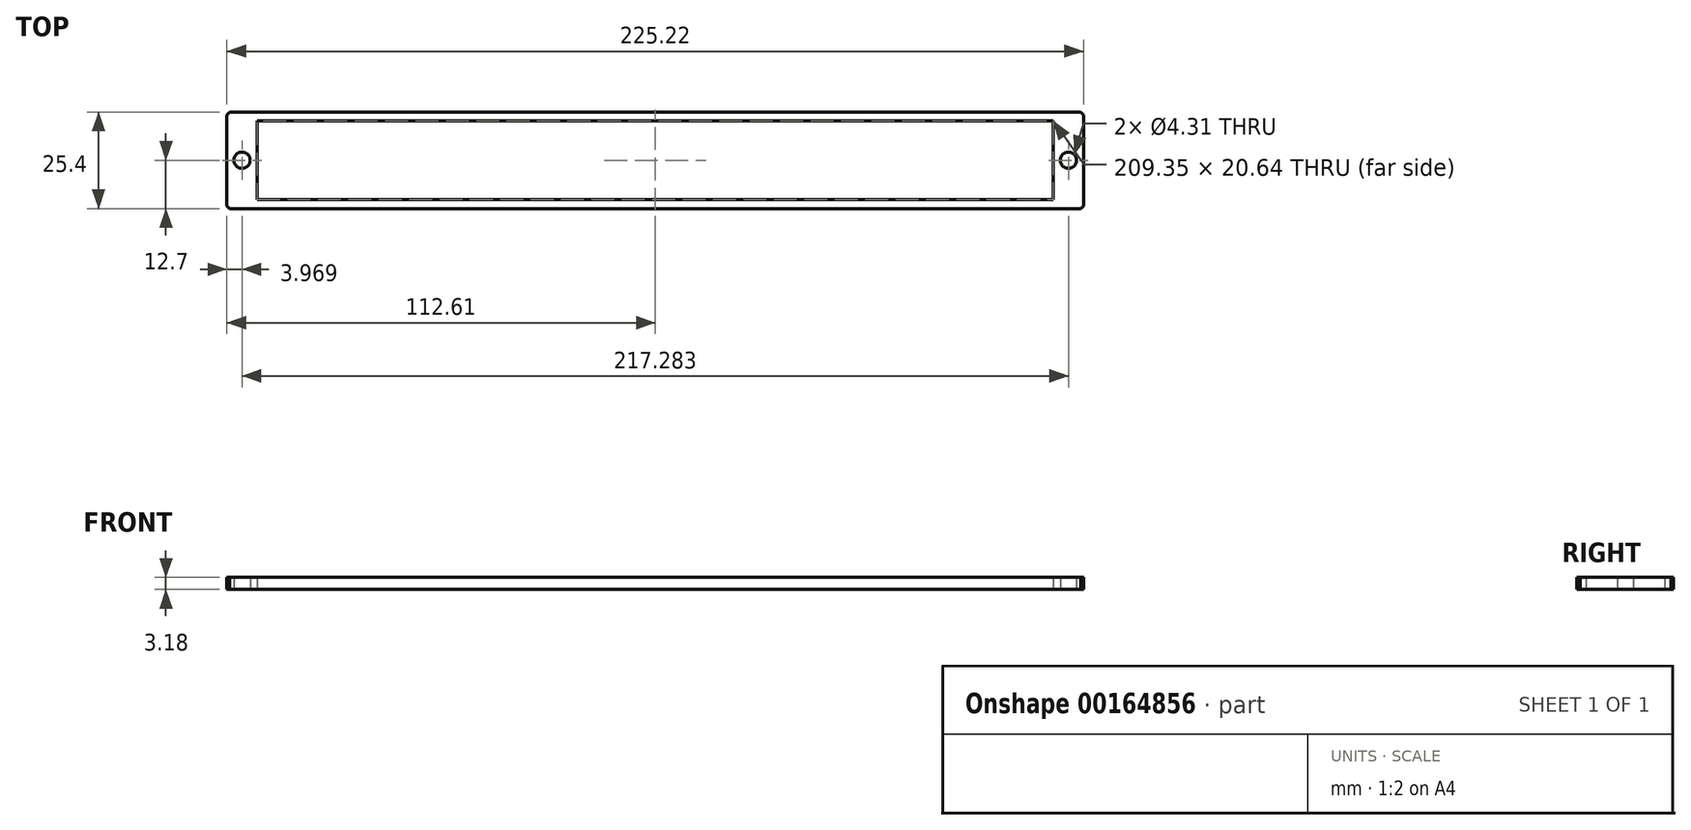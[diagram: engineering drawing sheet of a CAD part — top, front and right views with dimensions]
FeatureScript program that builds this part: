
annotation { "Feature Type Name" : "Feature", "Feature Type Description" : "" }
export const myFeature = defineFeature(function(context is Context, id is Id, definition is map)
    precondition{}
    {
        {
            var Q0;
            Q0=qCreatedBy(makeId("Top.planeOp"),FACE);
            var sketch = newSketch(context, id + "F0", { "sketchPlane" : qUnion([Q0])});
            skLineSegment(sketch, "E0.bottom", {"start": v(104.67, 10.32) * mm, "end": v(-104.67, 10.32) * mm});
            skLineSegment(sketch, "E0.top", {"start": v(104.67, -10.32) * mm, "end": v(-104.67, -10.32) * mm});
            skLineSegment(sketch, "E0.left", {"start": v(104.67, 10.32) * mm, "end": v(104.67, -10.32) * mm});
            skLineSegment(sketch, "E0.right", {"start": v(-104.67, 10.32) * mm, "end": v(-104.67, -10.32) * mm});
            skPoint(sketch, "E0.middle", {"position": v(0, 0) * mm});
            skLineSegment(sketch, "E1.bottom", {"start": v(112.61, 12.7) * mm, "end": v(-112.61, 12.7) * mm});
            skLineSegment(sketch, "E1.top", {"start": v(112.61, -12.7) * mm, "end": v(-112.61, -12.7) * mm});
            skLineSegment(sketch, "E1.left", {"start": v(112.61, 12.7) * mm, "end": v(112.61, -12.7) * mm});
            skLineSegment(sketch, "E1.right", {"start": v(-112.61, 12.7) * mm, "end": v(-112.61, -12.7) * mm});
            skLineSegment(sketch, "E2", {"start": v(-112.61, 0) * mm, "end": v(-108.64, 0) * mm, "construction": true});
            skLineSegment(sketch, "E3", {"start": v(-108.64, 0) * mm, "end": v(-104.67, 0) * mm, "construction": true});
            skLineSegment(sketch, "E4", {"start": v(104.67, 0) * mm, "end": v(108.64, 0) * mm, "construction": true});
            skLineSegment(sketch, "E5", {"start": v(108.64, 0) * mm, "end": v(112.61, 0) * mm, "construction": true});
            skCircle(sketch, "E6", {"center": v(-108.64, 0) * mm, "radius": 2.15 * mm});
            skCircle(sketch, "E7", {"center": v(108.64, 0) * mm, "radius": 2.15 * mm});
            skSolve(sketch);
        }
        {
            var Q0;
            Q0 = qSketchRegion(id + "F0", true);
            extrude(context, id + "F1", {"entities" : qUnion([Q0]), "depth" : 3.17 * mm});
        }
        {
            var Q0;
            Q0=makeQuery(id+"F1.opExtrude","SWEPT_EDGE",EDGE,{"disambiguationData":[OSD([sQuery(id+"F0.wireOp",EDGE,"E1.top"),sQuery(id+"F0.wireOp",EDGE,"E1.right")])]});
            var Q1;
            Q1=makeQuery(id+"F1.opExtrude","SWEPT_EDGE",EDGE,{"disambiguationData":[OSD([sQuery(id+"F0.wireOp",EDGE,"E1.bottom"),sQuery(id+"F0.wireOp",EDGE,"E1.right")])]});
            var Q2;
            Q2=makeQuery(id+"F1.opExtrude","SWEPT_EDGE",EDGE,{"disambiguationData":[OSD([sQuery(id+"F0.wireOp",EDGE,"E1.top"),sQuery(id+"F0.wireOp",EDGE,"E1.left")])]});
            var Q3;
            Q3=makeQuery(id+"F1.opExtrude","SWEPT_EDGE",EDGE,{"disambiguationData":[OSD([sQuery(id+"F0.wireOp",EDGE,"E1.bottom"),sQuery(id+"F0.wireOp",EDGE,"E1.left")])]});
            chamfer(context, id + "F2", {"entities" : qUnion([Q0, Q1, Q2, Q3]), "width" : 0.76 * mm, "tangentPropagation" : true});
        }
    });
